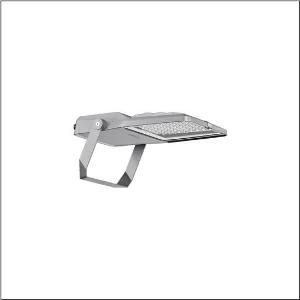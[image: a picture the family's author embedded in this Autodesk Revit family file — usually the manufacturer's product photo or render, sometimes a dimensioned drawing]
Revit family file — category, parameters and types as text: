
# Revit family: floodlight_fl_21_mini___pl43_5xa7773c2a1a_a3ea
name_source: partatom
category: Lighting Fixtures
units: mm (PartAtom-declared; Revit-internal decimal feet)

## family parameters
Cut with Voids When Loaded = No
Host = Face
Light Source = No
Part Type = Normal
Room Calculation Point = No
Round Connector Dimension = Use Diameter
Shared = No

## types (1)
- --- (1 x LED, 20010 lm, 163.5 W, 3000K)
    Apparent Load = 163 VA
    CIE Flux Codes = 27 78 99 100 100
    Color Rendering = 70
    Color Temperature = 3000K
    Default Elevation = 1800 mm
    Description = Floodlight FL 21 mini, floodlight, primary light control with lens, of PMMA, primary optical cover: protective disc, of toughened safety glass, transparent, light distribution: PL43, light emission: direct distribution, installation type: surface-mounted, LED, High Power LED, rated luminous flux: 20.010lm, luminous efficacy: 122lm/W, light colour: 730, colour temperature: 3000K, control gear: ON/OFF Multilumen, control: pre-setting: linear dimming characteristic, Temp-Guard, with terminal, 6-pole, mains connection: 220..240V, AC, 50/60Hz, start of lifetime: 164W, luminaire housing, of diecast aluminium, powder-coated, SITECO metallic grey (DB 702S), corrosivity category C5 mid according to DIN EN ISO 12944, suitable for swimming pools, chlorine-resistant, sealing non-destructively replaceable, mounting bracket, of steel, galvanised, powder-coated, SITECO metallic grey (DB 702S), ON/OFF, protection rating (complete): IP66, insulation class (complete): insulation class I (protective earthing), certification: CE, ENEC, VDE, protection symbol: D, impact resistance: IK08, permissible operating ambient temperature: -40..+40°C, permissible operating ambient temperature for outdoor applications: -40..+50°C, standard: DIN EN 12944, LABS conformity tested according to VDMA 24364:2018-05, packaging unit: 1 piece

Light Distribution: PL43
    Height = 70 mm
    Lamp = 1 x LED
    Lamp Light Flux = 20010 lm
    Lamp Power = 163.5 W
    Lamp count = 1
    Length = 485 mm
    Luminous efficacy = 122 lm/W
    Manufacturer = Siteco
    ModVariant = No
    Model = 5XA7773C2A1A
    Mounting Place = Pole
    Mounting Type = Pole annexe
    Number of Poles = 1
    OnlyDefault = Yes
    Power Factor = 1
    Product Name = Floodlight FL 21 mini | PL43
    Product group = floodlight | pylon annexe
    ProductGroupID = 6201
    Protection Class = Protection class I
    Protection Degree = IP 66
    RLX_Detail_Level = 1
    RLX_Emergency_Light_Flux = 0 lm
    RLX_Emergency_Type = 0
    RLX_Emergency_Type_DB = No
    RlxData = <blob elided: 94237 chars, md5=f26497ae>
    Socket = socket
    Standby Power = 0 W
    System Light Flux = 20010 lm
    System Power = 163 W
    Type Comments = factory setting: luminous flux: 100 % | (ON | - | - | - | - | - | - | -) | 825 mA
    Type Image = l_1006845.jpg
    URL = http://relux.com
    VarID = @adj_163395
    Voltage = 0 V
    Weight = 0.00 kg
    Width = 337 mm

## geometry (parser evidence)
native form markers: Blend x4, Sweep x13
no freeform markers — native parametric forms only
